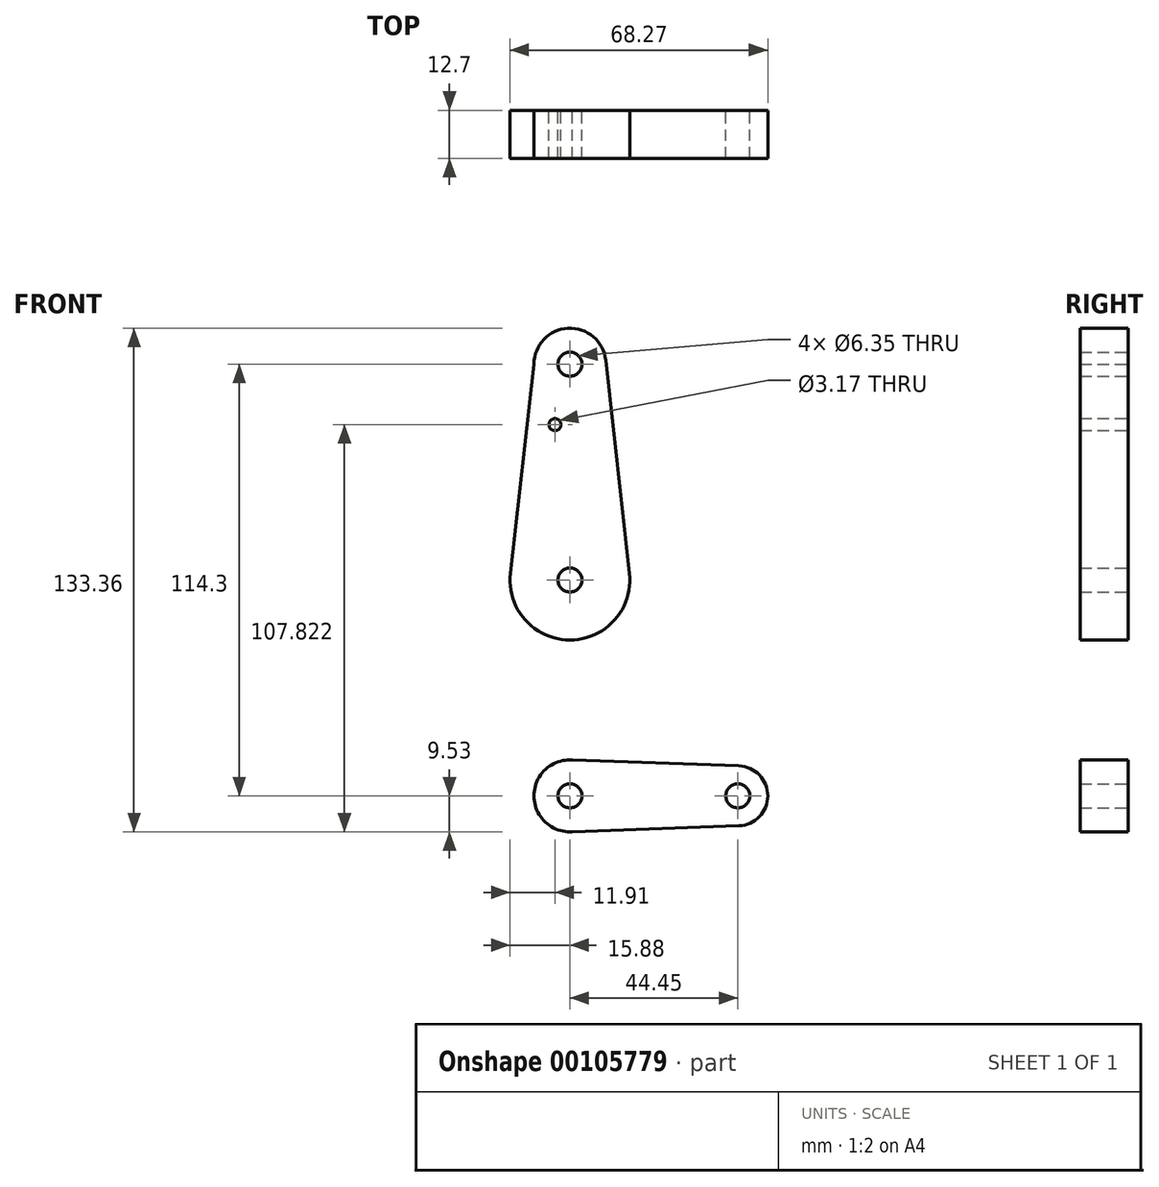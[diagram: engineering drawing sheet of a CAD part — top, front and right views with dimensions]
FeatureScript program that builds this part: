
annotation { "Feature Type Name" : "Feature", "Feature Type Description" : "" }
export const myFeature = defineFeature(function(context is Context, id is Id, definition is map)
    precondition{}
    {
        {
            var Q0;
            Q0=qCreatedBy(makeId("Front.planeOp"),FACE);
            var sketch = newSketch(context, id + "F0", { "sketchPlane" : qUnion([Q0])});
            skLineSegment(sketch, "E0", {"start": v(0, 0) * mm, "end": v(0, 114.3) * mm, "construction": true});
            skCircle(sketch, "E1", {"center": v(0, 114.3) * mm, "radius": 9.53 * mm});
            skCircle(sketch, "E2", {"center": v(0, 57.15) * mm, "radius": 15.88 * mm});
            skCircle(sketch, "E3", {"center": v(0, 0) * mm, "radius": 9.53 * mm});
            skLineSegment(sketch, "E4", {"start": v(0, 0) * mm, "end": v(44.45, 0) * mm, "construction": true});
            skCircle(sketch, "E5", {"center": v(44.45, 0) * mm, "radius": 7.94 * mm});
            skLineSegment(sketch, "E6", {"start": v(-9.52, 114.3) * mm, "end": v(-15.77, 58.93) * mm});
            skLineSegment(sketch, "E7", {"start": v(9.47, 115.36) * mm, "end": v(15.78, 58.91) * mm});
            skLineSegment(sketch, "E8", {"start": v(-15.78, 55.39) * mm, "end": v(-9.58, 0) * mm});
            skLineSegment(sketch, "E9", {"start": v(15.52, 53.12) * mm, "end": v(9.58, 0) * mm});
            skLineSegment(sketch, "E10", {"start": v(0, 9.53) * mm, "end": v(44.73, 7.93) * mm});
            skLineSegment(sketch, "E11", {"start": v(0, -9.53) * mm, "end": v(44.73, -7.93) * mm});
            skCircle(sketch, "E12", {"center": v(0, 114.3) * mm, "radius": 3.17 * mm});
            skCircle(sketch, "E13", {"center": v(0, 57.15) * mm, "radius": 3.18 * mm});
            skCircle(sketch, "E14", {"center": v(0, 0) * mm, "radius": 3.18 * mm});
            skCircle(sketch, "E15", {"center": v(44.45, 0) * mm, "radius": 3.18 * mm});
            skCircle(sketch, "E16", {"center": v(-3.97, 98.3) * mm, "radius": 1.59 * mm});
            skSolve(sketch);
        }
        {
            var Q0;
            Q0 = qSketchRegion(id + "F0", true);
            extrude(context, id + "F1", {"entities" : qUnion([Q0]), "depth" : 12.7 * mm});
        }
    });
